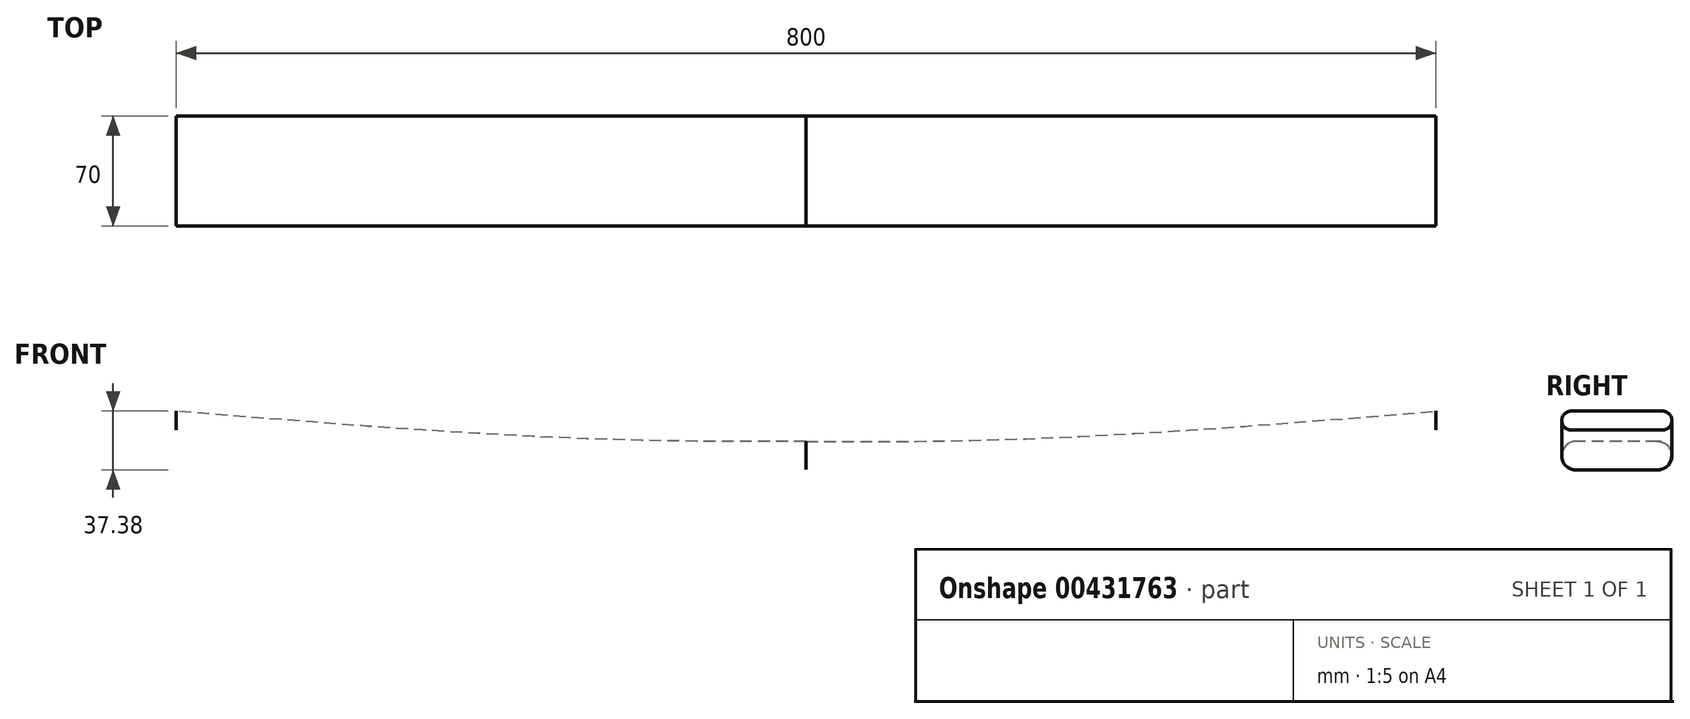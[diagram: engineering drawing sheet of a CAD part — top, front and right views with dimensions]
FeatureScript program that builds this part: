
annotation { "Feature Type Name" : "Feature", "Feature Type Description" : "" }
export const myFeature = defineFeature(function(context is Context, id is Id, definition is map)
    precondition{}
    {
        {
            var Q0;
            Q0=qCreatedBy(makeId("Right.planeOp"),FACE);
            var sketch = newSketch(context, id + "F0", { "sketchPlane" : qUnion([Q0])});
            skLineSegment(sketch, "E0.bottom", {"start": v(26, 9) * mm, "end": v(-26, 9) * mm});
            skLineSegment(sketch, "E0.top", {"start": v(26, -9) * mm, "end": v(-26, -9) * mm});
            skPoint(sketch, "E0.middle", {"position": v(0, 0) * mm});
            skArc(sketch, "E1", {"start": v(-26, 9) * mm, "mid": v(-35, 0) * mm, "end": v(-26, -9) * mm});
            skArc(sketch, "E2.MirrorCS", {"start": v(26, 9) * mm, "mid": v(35, 0) * mm, "end": v(26, -9) * mm});
            skLineSegment(sketch, "E3", {"start": v(0, 0) * mm, "end": v(0, -31.44) * mm, "construction": true});
            skPoint(sketch, "E3.endSnap0", {"position": v(0, -9) * mm});
            skLineSegment(sketch, "E4", {"start": v(0, 0) * mm, "end": v(0, 19.21) * mm, "construction": true});
            skPoint(sketch, "E4.endSnap0", {"position": v(0, 9) * mm});
            skSolve(sketch);
        }
        {
            var Q0;
            Q0=qCreatedBy(makeId("Right.planeOp"),FACE);
            cPlane(context, id + "F1", {"entities" : qUnion([Q0]), "cplaneType" : CPlaneType.OFFSET, "offset" : 400 * mm, "oppositeDirection" : true, "width" : 150 * mm, "height" : 150 * mm});
        }
        {
            var Q0;
            Q0=qCreatedBy(id+"F1.planeOp",FACE);
            var sketch = newSketch(context, id + "F2", { "sketchPlane" : qUnion([Q0])});
            skLineSegment(sketch, "E5", {"start": v(-29, 28.17) * mm, "end": v(29, 28.17) * mm});
            skLineSegment(sketch, "E6", {"start": v(-29, 28.17) * mm, "end": v(-29, 22.17) * mm, "construction": true});
            skLineSegment(sketch, "E7", {"start": v(29, 28.17) * mm, "end": v(29, 22.17) * mm, "construction": true});
            skLineSegment(sketch, "E8", {"start": v(-29, 22.17) * mm, "end": v(29, 22.17) * mm, "construction": true});
            skLineSegment(sketch, "E9.MirrorCS", {"start": v(-29, 16.17) * mm, "end": v(29, 16.17) * mm});
            skArc(sketch, "E10", {"start": v(-29, 28.17) * mm, "mid": v(-35, 22.17) * mm, "end": v(-29, 16.17) * mm});
            skArc(sketch, "E11", {"start": v(29, 28.17) * mm, "mid": v(35, 22.17) * mm, "end": v(29, 16.17) * mm});
            skLineSegment(sketch, "E12", {"start": v(0, 22.17) * mm, "end": v(0, 28.17) * mm, "construction": true});
            skSolve(sketch);
        }
        {
            var Q0;
            Q0=qCreatedBy(makeId("Right.planeOp"),FACE);
            cPlane(context, id + "F3", {"entities" : qUnion([Q0]), "cplaneType" : CPlaneType.OFFSET, "offset" : 70 * mm, "oppositeDirection" : true, "width" : 150 * mm, "height" : 150 * mm});
        }
        {
            var Q0;
            Q0=qCreatedBy(id+"F3.planeOp",FACE);
            var sketch = newSketch(context, id + "F4", { "sketchPlane" : qUnion([Q0])});
            skLineSegment(sketch, "E13.bottom", {"start": v(26, 9) * mm, "end": v(-26, 9) * mm});
            skLineSegment(sketch, "E13.top", {"start": v(26, -9) * mm, "end": v(-26, -9) * mm});
            skPoint(sketch, "E13.middle", {"position": v(0, 0) * mm});
            skArc(sketch, "E14", {"start": v(-26, 9) * mm, "mid": v(-35, 0) * mm, "end": v(-26, -9) * mm});
            skArc(sketch, "E15.MirrorCS", {"start": v(26, 9) * mm, "mid": v(35, 0) * mm, "end": v(26, -9) * mm});
            skSolve(sketch);
        }
        {
            var Q0;
            Q0=makeQuery(id+"F0.imprint","IMPRINT",FACE,{"disambiguationData":[TD([[makeQuery(id+"F0.imprint","IMPRINT",EDGE,{"derivedFrom":sQuery(id+"F0.wireOp",EDGE,"E0.bottom")}),1.0]])]});
            var Q1;
            Q1=makeQuery(id+"F4.imprint","IMPRINT",FACE,{"disambiguationData":[TD([[makeQuery(id+"F4.imprint","IMPRINT",EDGE,{"derivedFrom":sQuery(id+"F4.wireOp",EDGE,"E13.bottom")}),1.0]])]});
            var Q2;
            Q2=makeQuery(id+"F2.imprint","IMPRINT",FACE,{"disambiguationData":[TD([[makeQuery(id+"F2.imprint","IMPRINT",EDGE,{"derivedFrom":sQuery(id+"F2.wireOp",EDGE,"E5")}),-1.0]])]});
            loft(context, id + "F5", {"sheetProfilesArray" : [{ "sheetProfileEntities" : qUnion([Q0]) }, { "sheetProfileEntities" : qUnion([Q1]) }, { "sheetProfileEntities" : qUnion([Q2]) }]});
        }
        {
            var Q0;
            Q0=qCreatedBy(makeId("Right.planeOp"),FACE);
            cPlane(context, id + "F6", {"entities" : qUnion([Q0]), "cplaneType" : CPlaneType.OFFSET, "offset" : 70 * mm, "width" : 150 * mm, "height" : 150 * mm});
        }
        {
            var Q0;
            Q0=qCreatedBy(id+"F6.planeOp",FACE);
            var sketch = newSketch(context, id + "F7", { "sketchPlane" : qUnion([Q0])});
            skLineSegment(sketch, "E16.bottom", {"start": v(26, 9) * mm, "end": v(-26, 9) * mm});
            skLineSegment(sketch, "E16.top", {"start": v(26, -9) * mm, "end": v(-26, -9) * mm});
            skPoint(sketch, "E16.middle", {"position": v(0, 0) * mm});
            skArc(sketch, "E17", {"start": v(-26, 9) * mm, "mid": v(-35, 0) * mm, "end": v(-26, -9) * mm});
            skArc(sketch, "E18.MirrorCS", {"start": v(26, 9) * mm, "mid": v(35, 0) * mm, "end": v(26, -9) * mm});
            skSolve(sketch);
        }
        {
            var Q0;
            Q0=qCreatedBy(makeId("Right.planeOp"),FACE);
            cPlane(context, id + "F8", {"entities" : qUnion([Q0]), "cplaneType" : CPlaneType.OFFSET, "offset" : 400 * mm, "width" : 150 * mm, "height" : 150 * mm});
        }
        {
            var Q0;
            Q0=qCreatedBy(id+"F8.planeOp",FACE);
            var sketch = newSketch(context, id + "F9", { "sketchPlane" : qUnion([Q0])});
            skLineSegment(sketch, "E19", {"start": v(-29, 16.2) * mm, "end": v(29, 16.2) * mm});
            skLineSegment(sketch, "E20", {"start": v(-29, 28.2) * mm, "end": v(29, 28.2) * mm});
            skArc(sketch, "E21", {"start": v(-29, 28.2) * mm, "mid": v(-35, 22.2) * mm, "end": v(-29, 16.2) * mm});
            skArc(sketch, "E22", {"start": v(29, 28.2) * mm, "mid": v(35, 22.2) * mm, "end": v(29, 16.2) * mm});
            skSolve(sketch);
        }
        {
            var Q1;
            Q1=makeQuery(id+"F0.imprint","IMPRINT",FACE,{"disambiguationData":[TD([[makeQuery(id+"F0.imprint","IMPRINT",EDGE,{"derivedFrom":sQuery(id+"F0.wireOp",EDGE,"E0.bottom")}),1.0]])]});
            var Q2;
            Q2=makeQuery(id+"F7.imprint","IMPRINT",FACE,{"disambiguationData":[TD([[makeQuery(id+"F7.imprint","IMPRINT",EDGE,{"derivedFrom":sQuery(id+"F7.wireOp",EDGE,"E16.bottom")}),1.0]])]});
            var Q3;
            Q3=makeQuery(id+"F9.imprint","IMPRINT",FACE,{"disambiguationData":[TD([[makeQuery(id+"F9.imprint","IMPRINT",EDGE,{"derivedFrom":sQuery(id+"F9.wireOp",EDGE,"E19")}),1.0]])]});
            loft(context, id + "F10", {"operationType" : NewBodyOperationType.ADD, "sheetProfilesArray" : [{ "sheetProfileEntities" : qUnion([Q1]) }, { "sheetProfileEntities" : qUnion([Q2]) }, { "sheetProfileEntities" : qUnion([Q3]) }]});
        }
    });
